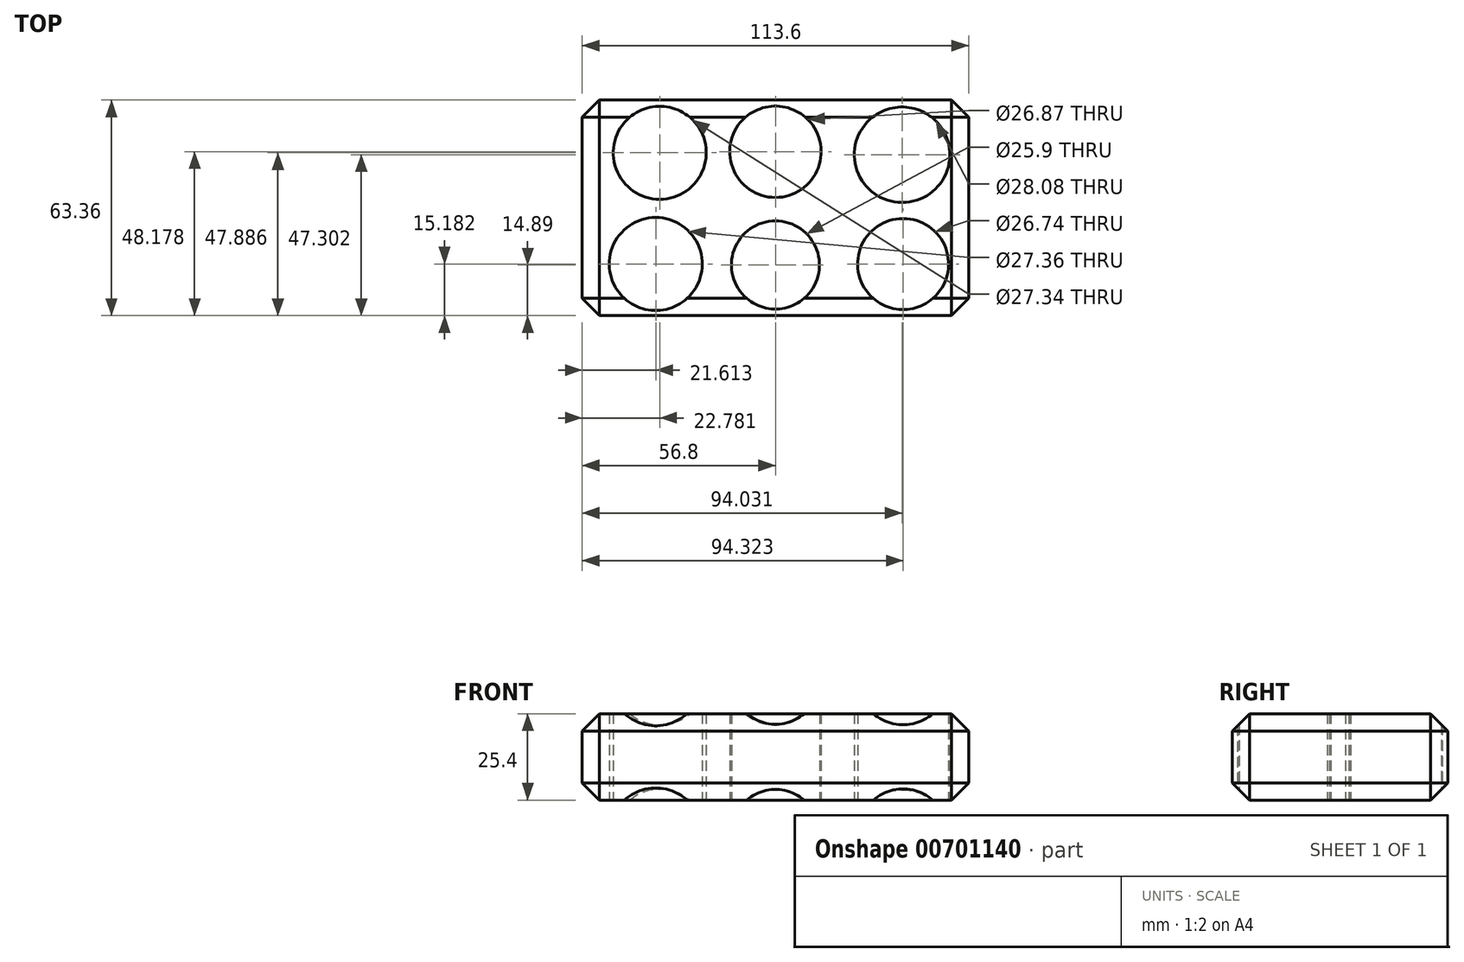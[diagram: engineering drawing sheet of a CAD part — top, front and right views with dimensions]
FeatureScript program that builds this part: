
annotation { "Feature Type Name" : "Feature", "Feature Type Description" : "" }
export const myFeature = defineFeature(function(context is Context, id is Id, definition is map)
    precondition{}
    {
        {
            var Q0;
            Q0=qCreatedBy(makeId("Top.planeOp"),FACE);
            var sketch = newSketch(context, id + "F0", { "sketchPlane" : qUnion([Q0])});
            skLineSegment(sketch, "E0.bottom", {"start": v(-56.8, 31.68) * mm, "end": v(56.8, 31.68) * mm});
            skLineSegment(sketch, "E0.top", {"start": v(-56.8, -31.68) * mm, "end": v(56.8, -31.68) * mm});
            skLineSegment(sketch, "E0.left", {"start": v(-56.8, 31.68) * mm, "end": v(-56.8, -31.68) * mm});
            skLineSegment(sketch, "E0.right", {"start": v(56.8, 31.68) * mm, "end": v(56.8, -31.68) * mm});
            skPoint(sketch, "E0.middle", {"position": v(0, 0) * mm});
            skCircle(sketch, "E1", {"center": v(0, 16.5) * mm, "radius": 13.43 * mm});
            skCircle(sketch, "E2", {"center": v(0, -16.8) * mm, "radius": 12.95 * mm});
            skCircle(sketch, "E3", {"center": v(37.23, 15.62) * mm, "radius": 14.04 * mm});
            skCircle(sketch, "E4", {"center": v(37.52, -16.5) * mm, "radius": 13.37 * mm});
            skCircle(sketch, "E5", {"center": v(-35.19, -16.5) * mm, "radius": 13.68 * mm});
            skCircle(sketch, "E6", {"center": v(-34.02, 16.2) * mm, "radius": 13.67 * mm});
            skSolve(sketch);
        }
        {
            var Q0;
            Q0=makeQuery(id+"F0.imprint","IMPRINT",FACE,{"disambiguationData":[TD([[makeQuery(id+"F0.imprint","IMPRINT",EDGE,{"derivedFrom":sQuery(id+"F0.wireOp",EDGE,"E0.bottom")}),-1.0]])]});
            extrude(context, id + "F1", {"entities" : qUnion([Q0]), "depth" : 25.4 * mm, "offsetDistance" : 25.4 * mm});
        }
        {
            var Q0;
            Q0=makeQuery(id+"F0.imprint","IMPRINT",FACE,{"disambiguationData":[TD([[makeQuery(id+"F0.imprint","IMPRINT",EDGE,{"derivedFrom":sQuery(id+"F0.wireOp",EDGE,"E0.bottom")}),-1.0]])]});
            var sketch = newSketch(context, id + "F2", { "sketchPlane" : qUnion([Q0])});
            skLineSegment(sketch, "E7.bottom", {"start": v(-54.82, -31.02) * mm, "end": v(54.82, -31.02) * mm});
            skLineSegment(sketch, "E7.top", {"start": v(-54.82, 31.02) * mm, "end": v(54.82, 31.02) * mm});
            skLineSegment(sketch, "E7.left", {"start": v(-54.82, -31.02) * mm, "end": v(-54.82, 31.02) * mm});
            skLineSegment(sketch, "E7.right", {"start": v(54.82, -31.02) * mm, "end": v(54.82, 31.02) * mm});
            skPoint(sketch, "E7.middle", {"position": v(0, 0) * mm});
            skSolve(sketch);
        }
        {
            var Q0;
            Q0=makeQuery(id+"F2.imprint","IMPRINT",FACE,{"disambiguationData":[TD([[makeQuery(id+"F2.imprint","IMPRINT",EDGE,{"derivedFrom":sQuery(id+"F2.wireOp",EDGE,"E7.bottom")}),1.0]])]});
            extrude(context, id + "F3", {"entities" : qUnion([Q0]), "operationType" : NewBodyOperationType.ADD, "depth" : 12.7 * mm, "offsetDistance" : 25.4 * mm});
        }
        {
            var Q0;
            Q0=makeQuery(id+"F1.opExtrude","CAP_EDGE",EDGE,{"disambiguationData":[OSD([sQuery(id+"F0.wireOp",EDGE,"E0.right")])],"isStart":true});
            var Q1;
            Q1=makeQuery(id+"F1.opExtrude","CAP_EDGE",EDGE,{"disambiguationData":[OSD([sQuery(id+"F0.wireOp",EDGE,"E0.bottom")])],"isStart":true});
            var Q2;
            Q2=makeQuery(id+"F1.opExtrude","CAP_EDGE",EDGE,{"disambiguationData":[OSD([sQuery(id+"F0.wireOp",EDGE,"E0.left")])],"isStart":true});
            var Q3;
            Q3=makeQuery(id+"F1.opExtrude","CAP_EDGE",EDGE,{"disambiguationData":[OSD([sQuery(id+"F0.wireOp",EDGE,"E0.top")])],"isStart":true});
            var Q4;
            Q4=makeQuery(id+"F1.opExtrude","SWEPT_EDGE",EDGE,{"disambiguationData":[OSD([sQuery(id+"F0.wireOp",EDGE,"E0.bottom"),sQuery(id+"F0.wireOp",EDGE,"E0.left")])]});
            var Q5;
            Q5=makeQuery(id+"F1.opExtrude","SWEPT_EDGE",EDGE,{"disambiguationData":[OSD([sQuery(id+"F0.wireOp",EDGE,"E0.top"),sQuery(id+"F0.wireOp",EDGE,"E0.right")])]});
            var Q6;
            Q6=makeQuery(id+"F1.opExtrude","CAP_EDGE",EDGE,{"disambiguationData":[OSD([sQuery(id+"F0.wireOp",EDGE,"E0.bottom")])],"isStart":false});
            var Q7;
            Q7=makeQuery(id+"F1.opExtrude","CAP_EDGE",EDGE,{"disambiguationData":[OSD([sQuery(id+"F0.wireOp",EDGE,"E0.left")])],"isStart":false});
            var Q8;
            Q8=makeQuery(id+"F1.opExtrude","SWEPT_EDGE",EDGE,{"disambiguationData":[OSD([sQuery(id+"F0.wireOp",EDGE,"E0.top"),sQuery(id+"F0.wireOp",EDGE,"E0.left")])]});
            var Q9;
            Q9=makeQuery(id+"F1.opExtrude","CAP_EDGE",EDGE,{"disambiguationData":[OSD([sQuery(id+"F0.wireOp",EDGE,"E0.top")])],"isStart":false});
            var Q10;
            Q10=makeQuery(id+"F1.opExtrude","CAP_EDGE",EDGE,{"disambiguationData":[OSD([sQuery(id+"F0.wireOp",EDGE,"E0.right")])],"isStart":false});
            var Q11;
            Q11=makeQuery(id+"F1.opExtrude","SWEPT_EDGE",EDGE,{"disambiguationData":[OSD([sQuery(id+"F0.wireOp",EDGE,"E0.bottom"),sQuery(id+"F0.wireOp",EDGE,"E0.right")])]});
            chamfer(context, id + "F4", {"entities" : qUnion([Q0, Q1, Q2, Q3, Q4, Q5, Q6, Q7, Q8, Q9, Q10, Q11]), "width" : 5.08 * mm, "tangentPropagation" : true});
        }
    });
